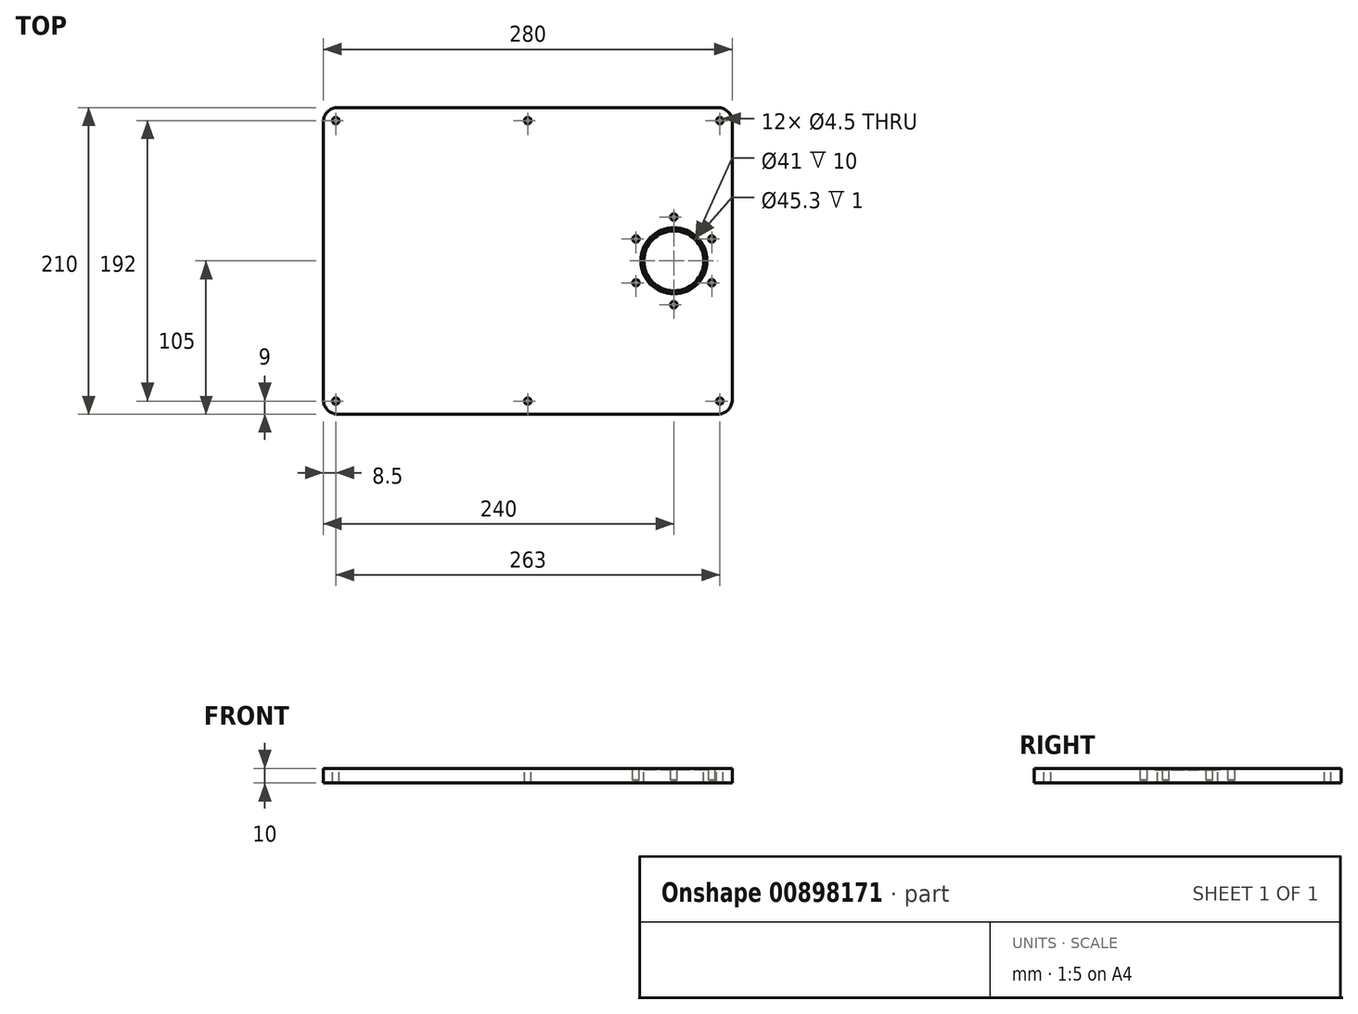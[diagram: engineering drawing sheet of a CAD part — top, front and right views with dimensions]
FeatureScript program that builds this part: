
annotation { "Feature Type Name" : "Feature", "Feature Type Description" : "" }
export const myFeature = defineFeature(function(context is Context, id is Id, definition is map)
    precondition{}
    {
        {
            var Q0;
            Q0=qCreatedBy(makeId("Top.planeOp"),FACE);
            var sketch = newSketch(context, id + "F0", { "sketchPlane" : qUnion([Q0])});
            skLineSegment(sketch, "E0.bottom", {"start": v(-140, 105) * mm, "end": v(140, 105) * mm});
            skLineSegment(sketch, "E0.top", {"start": v(-140, -105) * mm, "end": v(140, -105) * mm});
            skLineSegment(sketch, "E0.left", {"start": v(-140, 105) * mm, "end": v(-140, -105) * mm});
            skLineSegment(sketch, "E0.right", {"start": v(140, 105) * mm, "end": v(140, -105) * mm});
            skSolve(sketch);
        }
        {
            var Q0;
            Q0=makeQuery(id+"F0.imprint","IMPRINT",FACE,{"disambiguationData":[TD([[makeQuery(id+"F0.imprint","IMPRINT",EDGE,{"derivedFrom":sQuery(id+"F0.wireOp",EDGE,"E0.bottom")}),-1.0]])]});
            extrude(context, id + "F1", {"entities" : qUnion([Q0]), "depth" : 10 * mm, "offsetDistance" : 25 * mm});
        }
        {
            var Q0;
            Q0=makeQuery(id+"F1.opExtrude","CAP_FACE",FACE,{"disambiguationData":[OSD([sQuery(id+"F0.wireOp",EDGE,"E0.bottom"),sQuery(id+"F0.wireOp",EDGE,"E0.top"),sQuery(id+"F0.wireOp",EDGE,"E0.left"),sQuery(id+"F0.wireOp",EDGE,"E0.right")])],"isStart":false});
            var sketch = newSketch(context, id + "F2", { "sketchPlane" : qUnion([Q0])});
            skCircle(sketch, "E1", {"center": v(100, 0) * mm, "radius": 20.5 * mm});
            skCircle(sketch, "E2", {"center": v(100, 0) * mm, "radius": 30 * mm, "construction": true});
            skCircle(sketch, "E3", {"center": v(100, 0) * mm, "radius": 22.65 * mm});
            skCircle(sketch, "E4", {"center": v(100, 0) * mm, "radius": 21.35 * mm});
            skLineSegment(sketch, "E5", {"start": v(100, 0) * mm, "end": v(100, 30) * mm, "construction": true});
            skPoint(sketch, "E6", {"position": v(74.02, 15) * mm});
            skPoint(sketch, "E7", {"position": v(74.02, -15) * mm});
            skPoint(sketch, "E8", {"position": v(100, -30) * mm});
            skPoint(sketch, "E9", {"position": v(125.98, -15) * mm});
            skPoint(sketch, "E10", {"position": v(125.98, 15) * mm});
            skLineSegment(sketch, "E11", {"start": v(74.02, 15) * mm, "end": v(100, 0) * mm, "construction": true});
            skLineSegment(sketch, "E12", {"start": v(74.02, -15) * mm, "end": v(100, 0) * mm, "construction": true});
            skLineSegment(sketch, "E13", {"start": v(100, -30) * mm, "end": v(100, 0) * mm, "construction": true});
            skLineSegment(sketch, "E14", {"start": v(125.98, -15) * mm, "end": v(100, 0) * mm, "construction": true});
            skLineSegment(sketch, "E15", {"start": v(125.98, 15) * mm, "end": v(100, 0) * mm, "construction": true});
            skLineSegment(sketch, "E16", {"start": v(100, 30) * mm, "end": v(100, 0) * mm, "construction": true});
            skSolve(sketch);
        }
        {
            var Q0;
            Q0=makeQuery(id+"F2.imprint","IMPRINT",FACE,{"disambiguationData":[TD([[makeQuery(id+"F2.imprint","IMPRINT",EDGE,{"derivedFrom":sQuery(id+"F2.wireOp",EDGE,"E1")}),1.0]])]});
            extrude(context, id + "F3", {"entities" : qUnion([Q0]), "oppositeDirection" : true, "depth" : 10 * mm, "offsetDistance" : 25 * mm});
        }
        {
            var Q0;
            Q0=makeQuery(id+"F3.opExtrude","SWEPT_BODY",BODY,{"disambiguationData":[OSD([sQuery(id+"F2.wireOp",EDGE,"E1")])]});
            var Q1;
            Q1=makeQuery(id+"F1.opExtrude","SWEPT_BODY",BODY,{"disambiguationData":[OSD([sQuery(id+"F0.wireOp",EDGE,"E0.bottom"),sQuery(id+"F0.wireOp",EDGE,"E0.top"),sQuery(id+"F0.wireOp",EDGE,"E0.left"),sQuery(id+"F0.wireOp",EDGE,"E0.right")])]});
            booleanBodies(context, id + "F4", {"operationType" : BooleanOperationType.SUBTRACTION, "tools" : qUnion([Q0]), "targets" : qUnion([Q1])});
        }
        {
            var Q0;
            Q0=makeQuery(id+"F1.opExtrude","SWEPT_EDGE",EDGE,{"disambiguationData":[OSD([sQuery(id+"F0.wireOp",EDGE,"E0.bottom"),sQuery(id+"F0.wireOp",EDGE,"E0.left")])]});
            var Q1;
            Q1=makeQuery(id+"F1.opExtrude","SWEPT_EDGE",EDGE,{"disambiguationData":[OSD([sQuery(id+"F0.wireOp",EDGE,"E0.bottom"),sQuery(id+"F0.wireOp",EDGE,"E0.right")])]});
            var Q2;
            Q2=makeQuery(id+"F1.opExtrude","SWEPT_EDGE",EDGE,{"disambiguationData":[OSD([sQuery(id+"F0.wireOp",EDGE,"E0.top"),sQuery(id+"F0.wireOp",EDGE,"E0.right")])]});
            var Q3;
            Q3=makeQuery(id+"F1.opExtrude","SWEPT_EDGE",EDGE,{"disambiguationData":[OSD([sQuery(id+"F0.wireOp",EDGE,"E0.top"),sQuery(id+"F0.wireOp",EDGE,"E0.left")])]});
            fillet(context, id + "F5", {"entities" : qUnion([Q0, Q1, Q2, Q3]), "tangentPropagation" : true, "radius" : 10 * mm, "defaultsChanged" : true, "vertexSettings" : [], "allowEdgeOverflow" : false});
        }
        {
            var Q0;
            Q0=makeQuery(id+"F1.opExtrude","CAP_FACE",FACE,{"disambiguationData":[OSD([sQuery(id+"F0.wireOp",EDGE,"E0.bottom"),sQuery(id+"F0.wireOp",EDGE,"E0.top"),sQuery(id+"F0.wireOp",EDGE,"E0.left"),sQuery(id+"F0.wireOp",EDGE,"E0.right")])],"isStart":false});
            var sketch = newSketch(context, id + "F6", { "sketchPlane" : qUnion([Q0])});
            skPoint(sketch, "E17", {"position": v(-131.5, 96) * mm});
            skPoint(sketch, "E18.MirrorP", {"position": v(131.5, 96) * mm});
            skPoint(sketch, "E19.MirrorP", {"position": v(-131.5, -96) * mm});
            skPoint(sketch, "E20.MirrorP", {"position": v(131.5, -96) * mm});
            skPoint(sketch, "E21", {"position": v(0, 96) * mm});
            skPoint(sketch, "E22.MirrorP", {"position": v(0, -96) * mm});
            skSolve(sketch);
        }
        {
            var Q0;
            Q0=sQuery(id+"F6.wireOp",VERTEX,"E17");
            var Q1;
            Q1=sQuery(id+"F6.wireOp",VERTEX,"E21");
            var Q2;
            Q2=sQuery(id+"F6.wireOp",VERTEX,"E18.MirrorP");
            var Q3;
            Q3=sQuery(id+"F6.wireOp",VERTEX,"E20.MirrorP");
            var Q4;
            Q4=sQuery(id+"F6.wireOp",VERTEX,"E22.MirrorP");
            var Q5;
            Q5=sQuery(id+"F6.wireOp",VERTEX,"E19.MirrorP");
            var Q6;
            Q6=makeQuery(id+"F1.opExtrude","SWEPT_BODY",BODY,{"disambiguationData":[OSD([sQuery(id+"F0.wireOp",EDGE,"E0.bottom"),sQuery(id+"F0.wireOp",EDGE,"E0.top"),sQuery(id+"F0.wireOp",EDGE,"E0.left"),sQuery(id+"F0.wireOp",EDGE,"E0.right")])]});
            hole(context, id + "F7", {"style" : HoleStyle.SIMPLE, "endStyle" : HoleEndStyle.THROUGH, "standardTappedOrClearance" : lookupTablePath({ "fit" : "Normal", "standard" : "ISO", "size" : "M4", "type" : "Clearance" }), "standardBlindInLast" : lookupTablePath({ "fit" : "Normal", "standard" : "ISO", "engagement" : "75%", "pitch" : "0.7 mm", "size" : "M4", "type" : "Clearance & tapped" }), "holeDiameter" : 4.5 * mm, "majorDiameter" : 4 * mm, "tappedDepth" : 15 * mm, "tapClearance" : 3, "locations" : qUnion([Q0, Q1, Q2, Q3, Q4, Q5]), "scope" : qUnion([Q6])});
        }
        {
            var Q0;
            Q0=sQuery(id+"F2.wireOp",VERTEX,"E5.end");
            var Q1;
            Q1=sQuery(id+"F2.wireOp",VERTEX,"E15.start");
            var Q2;
            Q2=sQuery(id+"F2.wireOp",VERTEX,"E14.start");
            var Q3;
            Q3=sQuery(id+"F2.wireOp",VERTEX,"E13.start");
            var Q4;
            Q4=sQuery(id+"F2.wireOp",VERTEX,"E12.start");
            var Q5;
            Q5=sQuery(id+"F2.wireOp",VERTEX,"E11.start");
            var Q6;
            Q6=makeQuery(id+"F1.opExtrude","SWEPT_BODY",BODY,{"disambiguationData":[OSD([sQuery(id+"F0.wireOp",EDGE,"E0.bottom"),sQuery(id+"F0.wireOp",EDGE,"E0.top"),sQuery(id+"F0.wireOp",EDGE,"E0.left"),sQuery(id+"F0.wireOp",EDGE,"E0.right")])]});
            hole(context, id + "F8", {"style" : HoleStyle.SIMPLE, "endStyle" : HoleEndStyle.BLIND, "standardTappedOrClearance" : lookupTablePath({ "fit" : "Normal", "standard" : "ISO", "size" : "M4", "type" : "Clearance" }), "standardBlindInLast" : lookupTablePath({ "fit" : "Normal", "standard" : "ISO", "engagement" : "75%", "pitch" : "0.7 mm", "size" : "M4", "type" : "Clearance & tapped" }), "holeDiameter" : 4.5 * mm, "majorDiameter" : 5 * mm, "holeDepth" : 8 * mm, "tappedDepth" : 15 * mm, "tapClearance" : 3, "locations" : qUnion([Q0, Q1, Q2, Q3, Q4, Q5]), "scope" : qUnion([Q6])});
        }
        {
            var Q0;
            Q0=makeQuery(id+"F2.imprint","IMPRINT",FACE,{"disambiguationData":[TD([[makeQuery(id+"F2.imprint","IMPRINT",EDGE,{"derivedFrom":sQuery(id+"F2.wireOp",EDGE,"E3")}),1.0]])]});
            extrude(context, id + "F9", {"entities" : qUnion([Q0]), "oppositeDirection" : true, "depth" : 1 * mm, "offsetDistance" : 25 * mm});
        }
        {
            var Q0;
            Q0=makeQuery(id+"F9.opExtrude","SWEPT_BODY",BODY,{"disambiguationData":[OSD([sQuery(id+"F2.wireOp",EDGE,"E3"),sQuery(id+"F2.wireOp",EDGE,"E4")])]});
            var Q1;
            Q1=makeQuery(id+"F1.opExtrude","SWEPT_BODY",BODY,{"disambiguationData":[OSD([sQuery(id+"F0.wireOp",EDGE,"E0.bottom"),sQuery(id+"F0.wireOp",EDGE,"E0.top"),sQuery(id+"F0.wireOp",EDGE,"E0.left"),sQuery(id+"F0.wireOp",EDGE,"E0.right")])]});
            booleanBodies(context, id + "F10", {"operationType" : BooleanOperationType.SUBTRACTION, "tools" : qUnion([Q0]), "targets" : qUnion([Q1])});
        }
    });
